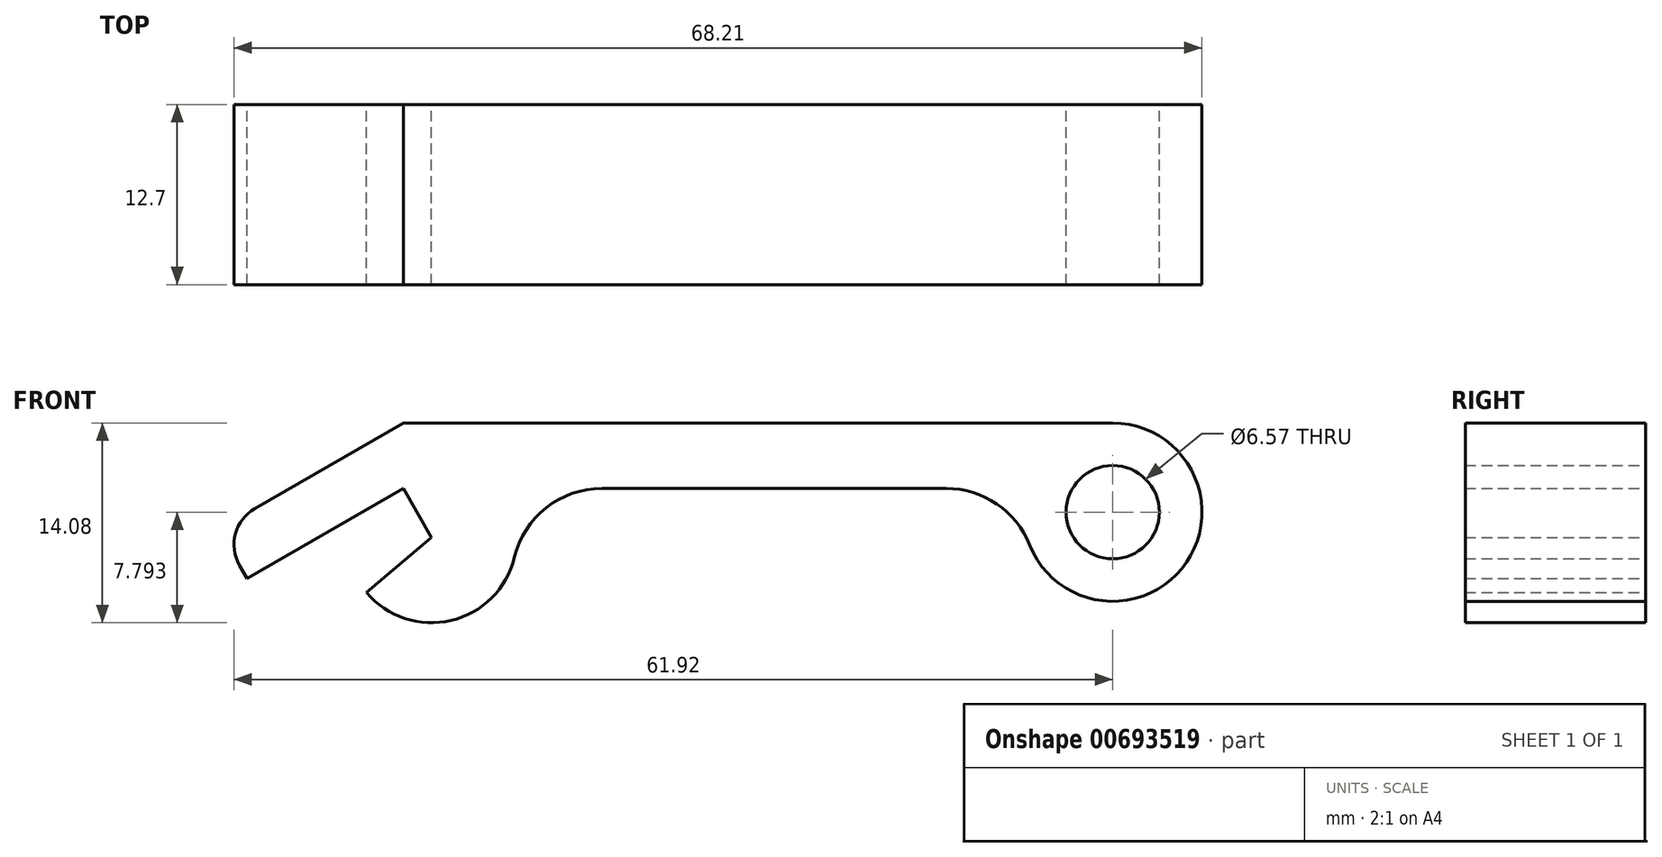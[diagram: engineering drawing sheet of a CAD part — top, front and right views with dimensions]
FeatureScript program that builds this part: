
annotation { "Feature Type Name" : "Feature", "Feature Type Description" : "" }
export const myFeature = defineFeature(function(context is Context, id is Id, definition is map)
    precondition{}
    {
        {
            var Q0;
            Q0=qCreatedBy(makeId("Front.planeOp"),FACE);
            var sketch = newSketch(context, id + "F0", { "sketchPlane" : qUnion([Q0])});
            skLineSegment(sketch, "E0", {"start": v(0, 0) * mm, "end": v(50, 0) * mm});
            skLineSegment(sketch, "E1", {"start": v(50, 0) * mm, "end": v(0, 0) * mm});
            skLineSegment(sketch, "E2", {"start": v(-10.46, -6.04) * mm, "end": v(0, 0) * mm});
            skLineSegment(sketch, "E3", {"start": v(-11.53, -10.03) * mm, "end": v(-11, -10.96) * mm});
            skLineSegment(sketch, "E4", {"start": v(-11, -10.96) * mm, "end": v(0, -4.62) * mm});
            skArc(sketch, "E5", {"start": v(50, 0) * mm, "mid": v(55.2, -9.81) * mm, "end": v(44.16, -8.62) * mm});
            skLineSegment(sketch, "E6", {"start": v(0, -4.62) * mm, "end": v(2, -8.08) * mm});
            skLineSegment(sketch, "E7", {"start": v(2, -8.08) * mm, "end": v(-2.6, -11.94) * mm});
            skArc(sketch, "E8", {"start": v(-2.6, -11.94) * mm, "mid": v(3.37, -13.92) * mm, "end": v(7.83, -9.48) * mm});
            skLineSegment(sketch, "E9", {"start": v(14, -4.62) * mm, "end": v(38.26, -4.62) * mm});
            skCircle(sketch, "E10", {"center": v(50, -6.29) * mm, "radius": 3.29 * mm});
            skPoint(sketch, "E11.visualSharp", {"position": v(-13, -7.5) * mm});
            skArc(sketch, "E11.filletArc", {"start": v(-10.46, -6.04) * mm, "mid": v(-11.82, -7.81) * mm, "end": v(-11.53, -10.03) * mm});
            skPoint(sketch, "E12.visualSharp", {"position": v(6.9, -4.62) * mm});
            skArc(sketch, "E12.filletArc", {"start": v(14, -4.62) * mm, "mid": v(10.08, -5.98) * mm, "end": v(7.83, -9.48) * mm});
            skPoint(sketch, "E13.visualSharp", {"position": v(43.94, -4.62) * mm});
            skArc(sketch, "E13.filletArc", {"start": v(44.16, -8.62) * mm, "mid": v(41.83, -5.71) * mm, "end": v(38.26, -4.62) * mm});
            skSolve(sketch);
        }
        {
            var Q0;
            Q0 = qSketchRegion(id + "F0", true);
            extrude(context, id + "F1", {"entities" : qUnion([Q0]), "depth" : 12.7 * mm, "offsetDistance" : 25.4 * mm});
        }
    });
